# Revit family: Waste_Receptacle-Bobrick-TrimLineSeries-B-35633
name_source: partatom
category: Specialty Equipment
units: mm (PartAtom-declared; Revit-internal decimal feet)

## family parameters
Cut with Voids When Loaded = No
Host = Face
OmniClass Number = 23.40.20.31
OmniClass Title = Refuse Disposal Furniture
Part Type = Normal
Room Calculation Point = No
Round Connector Dimension = Use Diameter
Shared = Yes

## types (1)
- B-35633
    ADA Compliant = Yes
    Assembly Code = E1090900
    Default Elevation = 47"
    Description = TrimLineSeries™ Recessed Waste Receptacle with Disposal Door
    Finish = Stainless Steel-Bobrick-Type 304-Satin
    Height = 28 1/8"
    Installation Type = Recessed
    Length = 4 7/16"
    Manufacturer = Bobrick Washroom Equipment, Inc.
    Materials = Stainless Steel-Bobrick-Type 304-Satin
    Model = B-35633
    Price = Prices may vary. Please consult Manufacturer Representative for most up-to-date price list.
    Product Documentation Link = https://www.bobrick.com
    Product Page URL = https://www.bobrick.com
    Revised Date = 11/03/2020
    Specification = Recessed waste receptacle with disposal door shall be Type-304 stainless steel with all-welded construction; exposed surfaces shall have satin fi nish. Door shall be Type-304, 18 gauge (1.2mm) secured to cabinet with a concealed, full-length stainless steel piano-hinge, cable door-swing limiter and equipped with a tumbler lock keyed like other Bobrick washroom accessories. Waste receptacle shall be Type-304, heavy-gauge stainless steel. All-welded construction with a capacity of 3-gal. (11.3-L).
    URL = http://bobrick.com
    Warranty Documentation Link = https://www.bobrick.com
    Warranty Information = 1 Year Limited Warranty
    Width = 14 1/8"

## geometry (parser evidence)
native form markers: Sweep x3
no freeform markers — native parametric forms only
